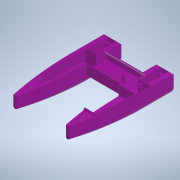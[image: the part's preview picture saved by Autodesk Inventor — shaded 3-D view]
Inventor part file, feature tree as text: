
AUTODESK INVENTOR PART (.ipt)
format: ipt  version: 2020.3 (Build 243373000, 373)  size: 1,104,896 bytes
history: native  units: mm
features: sketch x22, extrude x20, other x15, reference x13, chamfer x11, projected_geometry x11, plane x9, mirror x4, fillet x4, loft x1, direct_edit x1
ambient origin geometry x8: Origin, YZ Plane, XZ Plane, XY Plane, X Axis, Y Axis, Z Axis, Center Point
bodies: Solid1 (feature_tree)
feature tree (111):
  other  "Blocks"
  sketch  "Sketch1"  dims[d0=100.0mm d1=240.0mm]
  plane  "Work Plane1"
  plane  "Work Plane2"
  plane  "Work Plane3"
  plane  "Work Plane4"
  extrude  "Extrusion1"  Depth=240.0mm
  loft  "Loft3"
  chamfer  "Chamfer1"  Distance=10.0mm
  plane  "Work Plane7"
  mirror  "Mirror1"
  extrude  "Extrusion2"  Depth=13.217565mm
  extrude  "Extrusion3"  Depth=12.5mm
  extrude  "Extrusion4"  Depth=7.930539mm
  extrude  "Extrusion5"  Depth=10.0mm
  extrude  "Extrusion6"  Depth=3.0mm
  mirror  "Mirror2"
  plane  "Work Plane9"
  extrude  "Extrusion7"  Depth=5.0mm
  mirror  "Mirror3"
  extrude  "Extrusion8"  TaperAngle=0.0deg  [1 undecoded]
  extrude  "Extrusion9"  Depth=2.0mm TaperAngle=45.0deg
  chamfer  "Chamfer2"  Distance=10.0mm
  direct_edit  "Direct Edit1"
  extrude  "Extrusion10"  Depth=42.0mm
  extrude  "Extrusion11"  Depth=10.0mm TaperAngle=0.0deg
  extrude  "Extrusion12"  Depth=8.0mm
  extrude  "Extrusion13"  Depth=10.0mm TaperAngle=0.0deg
  extrude  "Extrusion14"  Depth=10.0mm
  plane  "Work Plane12"
  extrude  "Extrusion15"  Depth=10.0mm
  extrude  "Extrusion16"  Depth=10.0mm TaperAngle=0.0deg
  extrude  "Extrusion17"  TaperAngle=75.0deg  [1 undecoded]
  extrude  "Extrusion18"  Depth=10.0mm
  mirror  "Mirror5"
  fillet  "Fillet2"  Radius=10.0mm
  chamfer  "Chamfer3"  Distance=254.929mm
  fillet  "Fillet3"  Radius=10.0mm
  fillet  "Fillet4"  Radius=13.0mm
  chamfer  "Chamfer4"  Distance=140.0mm
  chamfer  "Chamfer5"  Distance=30.0mm
  chamfer  "Chamfer6"  Distance=3.0mm
  extrude  "Extrusion19"  Depth=10.0mm
  chamfer  "Chamfer7"  Distance=5.0mm
  chamfer  "Chamfer8"  Distance=15.0mm
  chamfer  "Chamfer9"  Distance=35.0mm
  fillet  "Fillet5"  Radius=2.5mm
  chamfer  "Chamfer10"  Distance=28.0mm
  chamfer  "Chamfer11"  Distance=8.0mm
  plane  "Work Plane14"
  extrude  "Extrusion20"  Depth=10.0mm TaperAngle=0.0deg
  sketch  "Sketch3"  dims[d2=280.0mm d3=30.0mm]
  sketch  "Sketch4"  dims[d4=50.0mm]
  other  "Edges3"
  plane  "Work Plane5"
  sketch  "Sketch5"  dims[d5=30.0mm]
  projected_geometry  "Projected Loop2"
  sketch  "Sketch6"  dims[d7=18.0mm]
  other  "Prindere servo"
  sketch  "Sketch7"  dims[d8=25.0mm]
  projected_geometry  "Projected Loop3"
  sketch  "Sketch8"  dims[d9=18.0mm]
  sketch  "Sketch9"  dims[d10=25.0mm d11=10.0mm d12=0.0mm]
  projected_geometry  "Projected Loop4"
  sketch  "Sketch12"  dims[d13=25.0mm d14=13.217565mm]
  sketch  "Sketch13"  dims[d16=7.930539mm d17=12.5mm]
  sketch  "Sketch14"  dims[d18=12.5mm d19=7.930539mm]
  sketch  "Sketch15"  dims[d24=10.0mm d25=5.0mm]
  sketch  "Sketch17"  dims[d26=3.0mm d27=3.0mm]
  reference  "Reference1"
  reference  "Reference2"
  reference  "Reference3"
  reference  "Reference4"
  reference  "Reference5"
  sketch  "Sketch18"  dims[d28=5.0mm d29=5.0mm]
  reference  "Reference6"
  reference  "Reference7"
  reference  "Reference8"
  reference  "Reference9"
  sketch  "Sketch19"  dims[d35=0.0mm d36=90.0deg d37=0.0mm d38=90.0deg]
  projected_geometry  "Projected Loop5"
  projected_geometry  "Projected Loop6"
  sketch  "Sketch20"  dims[d39=0.0mm d40=90.0deg d42=2.0mm d43=2.0mm d44=45.0deg]
  sketch  "Sketch22"  dims[d46=-100.0mm]
  projected_geometry  "Projected Loop7"
  projected_geometry  "Projected Loop8"
  projected_geometry  "Projected Loop9"
  projected_geometry  "Projected Loop10"
  projected_geometry  "Projected Loop11"
  sketch  "Sketch23"  dims[d47=30.0mm d48=10.0mm d49=0.0mm]
  reference  "Reference10"
  reference  "Reference11"
  sketch  "Sketch24"  dims[d97=22.0mm d98=42.0mm]
  sketch  "Sketch25"  dims[d99=10.0mm d100=45.0mm d101=0.0mm]
  projected_geometry  "Projected Loop12"
  sketch  "Sketch26"  dims[d102=8.0mm d103=8.0mm]
  other  "Work Axis2"
  sketch  "Sketch28"  dims[d104=12.0mm d105=0.0mm d106=40.0mm d107=0.0mm d108=7.0mm d109=20.0mm d110=5.0mm d111=0.0mm d118=75.0deg d119=6.5mm d120=10.0mm d121=254.929mm d122=0.0mm d124=10.0mm d125=13.0mm d126=140.0mm d127=30.0mm d128=3.0mm d129=5.0mm d130=5.0mm d131=15.0mm d132=35.0mm d133=0.0mm d136=2.5mm d137=28.0mm d138=8.0mm d139=25.0mm d140=0.0mm d141=44.0mm d142=2.0mm d143=1.396263mm d145=2.5mm d146=3.0mm d147=0.0mm d148=20.0mm d149=0.0mm d150=10.0mm d151=0.0mm d154=8.5mm d155=8.5mm d156=8.0mm d157=8.0mm d158=100.0mm d159=0.0mm d160=2.5mm d161=2.5mm d162=2.5mm d163=2.5mm d164=27.5mm d165=0.0mm d166=2.5mm d167=2.5mm d168=120.0mm d169=0.0mm d170=5.0mm d171=0.0mm d173=12.0mm d174=5.0mm d175=18.0mm d176=0.0mm d177=10.0mm d178=0.0mm d179=2.0mm d180=2.0mm d181=2.0mm d182=45.0deg d183=0.2mm d184=0.2mm d185=2.0mm d186=2.0mm d187=45.0deg d188=2.0mm d189=2.0mm d190=45.0deg d191=2.0mm d192=2.0mm d193=45.0deg d194=2.5mm d195=0.0mm d196=2.0mm d197=2.0mm d198=45.0deg d199=2.5mm d200=2.0mm d201=45.0deg d202=2.5mm d203=2.0mm d204=45.0deg d205=0.5mm d206=2.5mm d207=2.0mm d208=45.0deg d209=2.5mm d210=2.0mm d211=45.0deg d212=3.0mm d213=3.0mm d214=5.0mm d215=0.0mm]
  reference  "Reference12"
  reference  "Reference13"
  other  "Prindere servo:1"
  other  "Prindere servo:2"
  other  "Prindere servo:3"
  other  "Delete1"
  other  "<userpath>\Documents\Inventor\TheArch\R&D\Beta0\Structura\Prototip\Prototip1.iam"
  other  "Prototip1.iam"
  other  "MG996:3"
  other  "AnsambluMotor:1"
  other  "Prindere:1"
  other  "carma_v0:1"
  other  "carma_v0:2"
note: 2 required parameter values undecoded (feature->parameter linkage not recoverable at this tier; creation-order binding heuristic only, values carry confidence <= 0.55)
